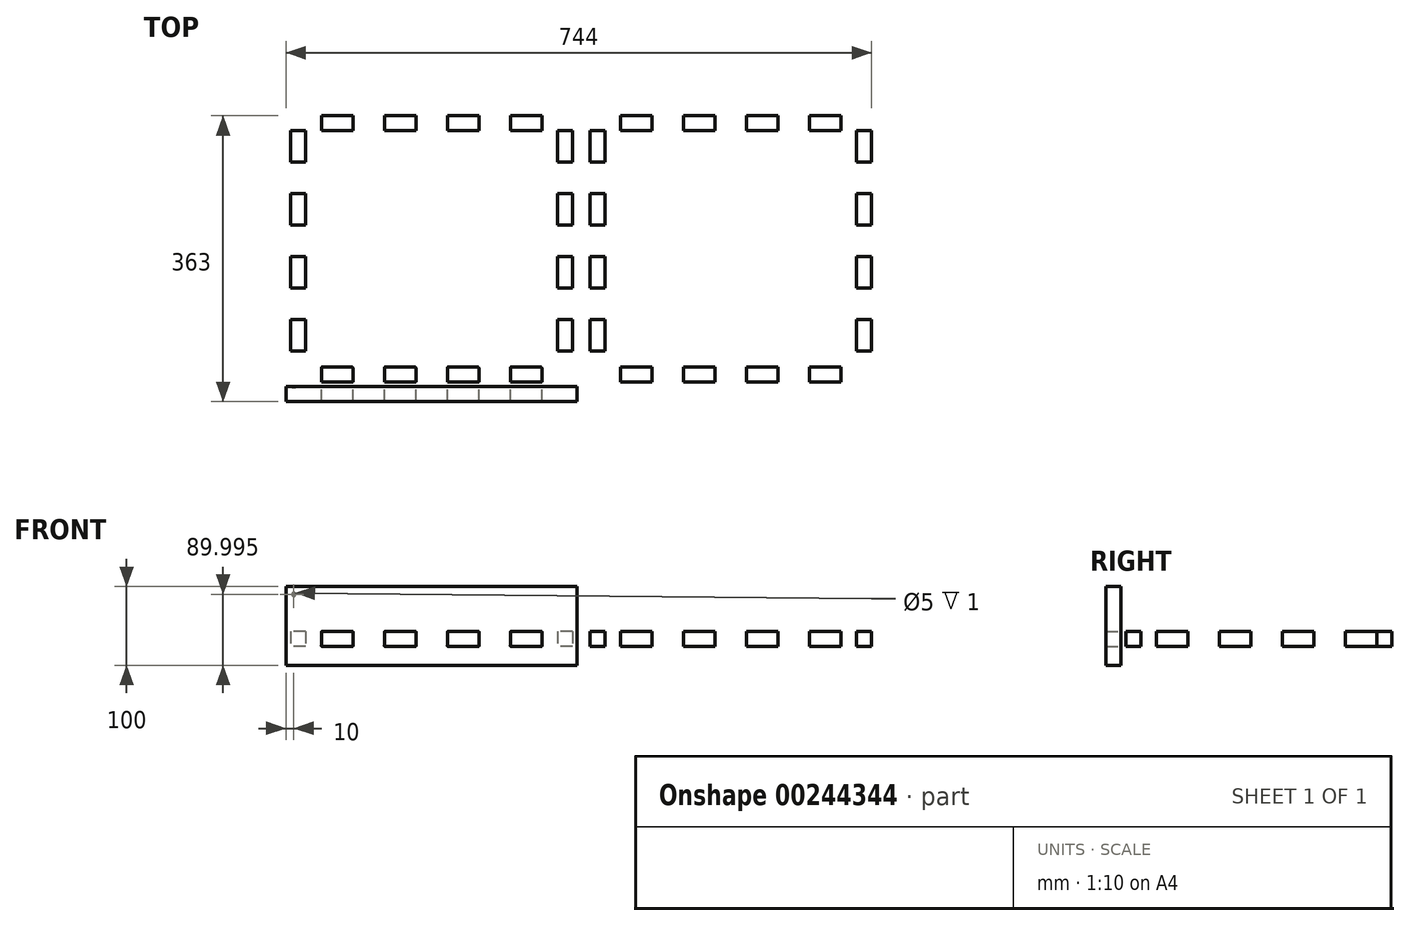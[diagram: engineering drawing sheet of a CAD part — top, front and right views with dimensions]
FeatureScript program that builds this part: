
annotation { "Feature Type Name" : "Feature", "Feature Type Description" : "" }
export const myFeature = defineFeature(function(context is Context, id is Id, definition is map)
    precondition{}
    {
        {
            var Q0;
            Q0=qCreatedBy(makeId("Top.planeOp"),FACE);
            var sketch = newSketch(context, id + "F0", { "sketchPlane" : qUnion([Q0])});
            skLineSegment(sketch, "E0.bottom", {"start": v(25, 25) * mm, "end": v(345, 25) * mm, "construction": true});
            skLineSegment(sketch, "E0.top", {"start": v(25, 325) * mm, "end": v(345, 325) * mm, "construction": true});
            skLineSegment(sketch, "E0.left", {"start": v(25, 25) * mm, "end": v(25, 325) * mm, "construction": true});
            skLineSegment(sketch, "E0.right", {"start": v(345, 25) * mm, "end": v(345, 325) * mm, "construction": true});
            skPoint(sketch, "E1", {"position": v(25, 25) * mm});
            skSolve(sketch);
        }
        {
            var Q0;
            Q0=qCreatedBy(makeId("Top.planeOp"),FACE);
            var sketch = newSketch(context, id + "F1", { "sketchPlane" : qUnion([Q0])});
            skPoint(sketch, "E2", {"position": v(25, 25) * mm});
            skLineSegment(sketch, "E3.bottom", {"start": v(25, 45) * mm, "end": v(6, 45) * mm});
            skLineSegment(sketch, "E3.top", {"start": v(25, 85) * mm, "end": v(6, 85) * mm});
            skLineSegment(sketch, "E3.left", {"start": v(25, 45) * mm, "end": v(25, 85) * mm});
            skLineSegment(sketch, "E3.right", {"start": v(6, 45) * mm, "end": v(6, 85) * mm});
            skLineSegment(sketch, "E4.0.1.0", {"start": v(25, 125) * mm, "end": v(6, 125) * mm});
            skLineSegment(sketch, "E4.0.1.1", {"start": v(6, 125) * mm, "end": v(6, 165) * mm});
            skLineSegment(sketch, "E4.0.1.2", {"start": v(25, 165) * mm, "end": v(6, 165) * mm});
            skLineSegment(sketch, "E4.0.1.3", {"start": v(25, 125) * mm, "end": v(25, 165) * mm});
            skLineSegment(sketch, "E4.0.2.0", {"start": v(25, 205) * mm, "end": v(6, 205) * mm});
            skLineSegment(sketch, "E4.0.2.1", {"start": v(6, 205) * mm, "end": v(6, 245) * mm});
            skLineSegment(sketch, "E4.0.2.2", {"start": v(25, 245) * mm, "end": v(6, 245) * mm});
            skLineSegment(sketch, "E4.0.2.3", {"start": v(25, 205) * mm, "end": v(25, 245) * mm});
            skLineSegment(sketch, "E4.0.3.0", {"start": v(25, 285) * mm, "end": v(6, 285) * mm});
            skLineSegment(sketch, "E4.0.3.1", {"start": v(6, 285) * mm, "end": v(6, 325) * mm});
            skLineSegment(sketch, "E4.0.3.2", {"start": v(25, 325) * mm, "end": v(6, 325) * mm});
            skLineSegment(sketch, "E4.0.3.3", {"start": v(25, 285) * mm, "end": v(25, 325) * mm});
            skLineSegment(sketch, "E4.1.0.0", {"start": v(364, 45) * mm, "end": v(345, 45) * mm});
            skLineSegment(sketch, "E4.1.0.1", {"start": v(345, 45) * mm, "end": v(345, 85) * mm});
            skLineSegment(sketch, "E4.1.0.2", {"start": v(364, 85) * mm, "end": v(345, 85) * mm});
            skLineSegment(sketch, "E4.1.0.3", {"start": v(364, 45) * mm, "end": v(364, 85) * mm});
            skLineSegment(sketch, "E4.1.1.0", {"start": v(364, 125) * mm, "end": v(345, 125) * mm});
            skLineSegment(sketch, "E4.1.1.1", {"start": v(345, 125) * mm, "end": v(345, 165) * mm});
            skLineSegment(sketch, "E4.1.1.2", {"start": v(364, 165) * mm, "end": v(345, 165) * mm});
            skLineSegment(sketch, "E4.1.1.3", {"start": v(364, 125) * mm, "end": v(364, 165) * mm});
            skLineSegment(sketch, "E4.1.2.0", {"start": v(364, 205) * mm, "end": v(345, 205) * mm});
            skLineSegment(sketch, "E4.1.2.1", {"start": v(345, 205) * mm, "end": v(345, 245) * mm});
            skLineSegment(sketch, "E4.1.2.2", {"start": v(364, 245) * mm, "end": v(345, 245) * mm});
            skLineSegment(sketch, "E4.1.2.3", {"start": v(364, 205) * mm, "end": v(364, 245) * mm});
            skLineSegment(sketch, "E4.1.3.0", {"start": v(364, 285) * mm, "end": v(345, 285) * mm});
            skLineSegment(sketch, "E4.1.3.1", {"start": v(345, 285) * mm, "end": v(345, 325) * mm});
            skLineSegment(sketch, "E4.1.3.2", {"start": v(364, 325) * mm, "end": v(345, 325) * mm});
            skLineSegment(sketch, "E4.1.3.3", {"start": v(364, 285) * mm, "end": v(364, 325) * mm});
            skLineSegment(sketch, "E4.direction1", {"start": v(6, 45) * mm, "end": v(345, 45) * mm, "construction": true});
            skLineSegment(sketch, "E4.direction2", {"start": v(6, 45) * mm, "end": v(6, 125) * mm, "construction": true});
            skLineSegment(sketch, "E5.bottom", {"start": v(45, 25) * mm, "end": v(85, 25) * mm});
            skLineSegment(sketch, "E5.top", {"start": v(45, 6) * mm, "end": v(85, 6) * mm});
            skLineSegment(sketch, "E5.left", {"start": v(45, 25) * mm, "end": v(45, 6) * mm});
            skLineSegment(sketch, "E5.right", {"start": v(85, 25) * mm, "end": v(85, 6) * mm});
            skLineSegment(sketch, "E6.0.1.0", {"start": v(45, 344) * mm, "end": v(45, 325) * mm});
            skLineSegment(sketch, "E6.0.1.1", {"start": v(45, 344) * mm, "end": v(85, 344) * mm});
            skLineSegment(sketch, "E6.0.1.2", {"start": v(45, 325) * mm, "end": v(85, 325) * mm});
            skLineSegment(sketch, "E6.0.1.3", {"start": v(85, 344) * mm, "end": v(85, 325) * mm});
            skLineSegment(sketch, "E6.1.0.0", {"start": v(125, 25) * mm, "end": v(125, 6) * mm});
            skLineSegment(sketch, "E6.1.0.1", {"start": v(125, 25) * mm, "end": v(165, 25) * mm});
            skLineSegment(sketch, "E6.1.0.2", {"start": v(125, 6) * mm, "end": v(165, 6) * mm});
            skLineSegment(sketch, "E6.1.0.3", {"start": v(165, 25) * mm, "end": v(165, 6) * mm});
            skLineSegment(sketch, "E6.1.1.0", {"start": v(125, 344) * mm, "end": v(125, 325) * mm});
            skLineSegment(sketch, "E6.1.1.1", {"start": v(125, 344) * mm, "end": v(165, 344) * mm});
            skLineSegment(sketch, "E6.1.1.2", {"start": v(125, 325) * mm, "end": v(165, 325) * mm});
            skLineSegment(sketch, "E6.1.1.3", {"start": v(165, 344) * mm, "end": v(165, 325) * mm});
            skLineSegment(sketch, "E6.2.0.0", {"start": v(205, 25) * mm, "end": v(205, 6) * mm});
            skLineSegment(sketch, "E6.2.0.1", {"start": v(205, 25) * mm, "end": v(245, 25) * mm});
            skLineSegment(sketch, "E6.2.0.2", {"start": v(205, 6) * mm, "end": v(245, 6) * mm});
            skLineSegment(sketch, "E6.2.0.3", {"start": v(245, 25) * mm, "end": v(245, 6) * mm});
            skLineSegment(sketch, "E6.2.1.0", {"start": v(205, 344) * mm, "end": v(205, 325) * mm});
            skLineSegment(sketch, "E6.2.1.1", {"start": v(205, 344) * mm, "end": v(245, 344) * mm});
            skLineSegment(sketch, "E6.2.1.2", {"start": v(205, 325) * mm, "end": v(245, 325) * mm});
            skLineSegment(sketch, "E6.2.1.3", {"start": v(245, 344) * mm, "end": v(245, 325) * mm});
            skLineSegment(sketch, "E6.3.0.0", {"start": v(285, 25) * mm, "end": v(285, 6) * mm});
            skLineSegment(sketch, "E6.3.0.1", {"start": v(285, 25) * mm, "end": v(325, 25) * mm});
            skLineSegment(sketch, "E6.3.0.2", {"start": v(285, 6) * mm, "end": v(325, 6) * mm});
            skLineSegment(sketch, "E6.3.0.3", {"start": v(325, 25) * mm, "end": v(325, 6) * mm});
            skLineSegment(sketch, "E6.3.1.0", {"start": v(285, 344) * mm, "end": v(285, 325) * mm});
            skLineSegment(sketch, "E6.3.1.1", {"start": v(285, 344) * mm, "end": v(325, 344) * mm});
            skLineSegment(sketch, "E6.3.1.2", {"start": v(285, 325) * mm, "end": v(325, 325) * mm});
            skLineSegment(sketch, "E6.3.1.3", {"start": v(325, 344) * mm, "end": v(325, 325) * mm});
            skLineSegment(sketch, "E6.direction1", {"start": v(45, 6) * mm, "end": v(125, 6) * mm, "construction": true});
            skLineSegment(sketch, "E6.direction2", {"start": v(45, 6) * mm, "end": v(45, 325) * mm, "construction": true});
            skLineSegment(sketch, "E7.bottom", {"start": v(25, 325) * mm, "end": v(345, 325) * mm});
            skLineSegment(sketch, "E7.top", {"start": v(25, 25) * mm, "end": v(345, 25) * mm});
            skLineSegment(sketch, "E7.left", {"start": v(25, 325) * mm, "end": v(25, 25) * mm});
            skLineSegment(sketch, "E7.right", {"start": v(345, 325) * mm, "end": v(345, 25) * mm});
            skLineSegment(sketch, "E8", {"start": v(540.47, -44.7) * mm, "end": v(540.47, -111.64) * mm, "construction": true});
            skSolve(sketch);
        }
        {
            var Q0;
            {var subQ0=sQuery(id+"F1.wireOp",EDGE,"E3.bottom");Q0=makeQuery(id+"F1.imprint","IMPRINT",FACE,{"disambiguationData":[TD([[makeQuery(id+"F1.imprint","IMPRINT",EDGE,{"derivedFrom":subQ0}),-1.0]])]});}
            var Q1;
            {var subQ0=sQuery(id+"F1.wireOp",EDGE,"E4.0.1.0");Q1=makeQuery(id+"F1.imprint","IMPRINT",FACE,{"disambiguationData":[TD([[makeQuery(id+"F1.imprint","IMPRINT",EDGE,{"derivedFrom":subQ0}),-1.0]])]});}
            var Q2;
            {var subQ15=sQuery(id+"F1.wireOp",EDGE,"E7.bottom");var subQ31=makeQuery(id+"F1.imprint","INTERSECT",VERTEX,{"derivedFrom":[sQuery(id+"F1.wireOp",EDGE,"E6.0.1.0"),subQ15]});Q2=makeQuery(id+"F1.imprint","IMPRINT",FACE,{"disambiguationData":[TD([[makeQuery(id+"F1.imprint","IMPRINT",EDGE,{"disambiguationData":[TD([[subQ31,-1.0]])],"derivedFrom":subQ15}),-1.0]])]});}
            var Q3;
            {var subQ0=sQuery(id+"F1.wireOp",EDGE,"E4.1.0.0");Q3=makeQuery(id+"F1.imprint","IMPRINT",FACE,{"disambiguationData":[TD([[makeQuery(id+"F1.imprint","IMPRINT",EDGE,{"derivedFrom":subQ0}),-1.0]])]});}
            var Q4;
            {var subQ0=sQuery(id+"F1.wireOp",EDGE,"E6.3.1.0");Q4=makeQuery(id+"F1.imprint","IMPRINT",FACE,{"disambiguationData":[TD([[makeQuery(id+"F1.imprint","IMPRINT",EDGE,{"derivedFrom":subQ0}),1.0]])]});}
            var Q5;
            {var subQ0=sQuery(id+"F1.wireOp",EDGE,"E4.0.2.0");Q5=makeQuery(id+"F1.imprint","IMPRINT",FACE,{"disambiguationData":[TD([[makeQuery(id+"F1.imprint","IMPRINT",EDGE,{"derivedFrom":subQ0}),-1.0]])]});}
            var Q6;
            {var subQ0=sQuery(id+"F1.wireOp",EDGE,"E4.0.3.0");Q6=makeQuery(id+"F1.imprint","IMPRINT",FACE,{"disambiguationData":[TD([[makeQuery(id+"F1.imprint","IMPRINT",EDGE,{"derivedFrom":subQ0}),-1.0]])]});}
            var Q7;
            {var subQ0=sQuery(id+"F1.wireOp",EDGE,"E4.1.2.0");Q7=makeQuery(id+"F1.imprint","IMPRINT",FACE,{"disambiguationData":[TD([[makeQuery(id+"F1.imprint","IMPRINT",EDGE,{"derivedFrom":subQ0}),-1.0]])]});}
            var Q8;
            {var subQ0=sQuery(id+"F1.wireOp",EDGE,"E4.1.1.0");Q8=makeQuery(id+"F1.imprint","IMPRINT",FACE,{"disambiguationData":[TD([[makeQuery(id+"F1.imprint","IMPRINT",EDGE,{"derivedFrom":subQ0}),-1.0]])]});}
            var Q9;
            {var subQ0=sQuery(id+"F1.wireOp",EDGE,"E6.3.0.0");Q9=makeQuery(id+"F1.imprint","IMPRINT",FACE,{"disambiguationData":[TD([[makeQuery(id+"F1.imprint","IMPRINT",EDGE,{"derivedFrom":subQ0}),1.0]])]});}
            var Q10;
            {var subQ0=sQuery(id+"F1.wireOp",EDGE,"E6.2.0.0");Q10=makeQuery(id+"F1.imprint","IMPRINT",FACE,{"disambiguationData":[TD([[makeQuery(id+"F1.imprint","IMPRINT",EDGE,{"derivedFrom":subQ0}),1.0]])]});}
            var Q11;
            {var subQ0=sQuery(id+"F1.wireOp",EDGE,"E6.1.1.0");Q11=makeQuery(id+"F1.imprint","IMPRINT",FACE,{"disambiguationData":[TD([[makeQuery(id+"F1.imprint","IMPRINT",EDGE,{"derivedFrom":subQ0}),1.0]])]});}
            var Q12;
            {var subQ0=sQuery(id+"F1.wireOp",EDGE,"E6.2.1.0");Q12=makeQuery(id+"F1.imprint","IMPRINT",FACE,{"disambiguationData":[TD([[makeQuery(id+"F1.imprint","IMPRINT",EDGE,{"derivedFrom":subQ0}),1.0]])]});}
            var Q13;
            {var subQ0=sQuery(id+"F1.wireOp",EDGE,"E6.1.0.0");Q13=makeQuery(id+"F1.imprint","IMPRINT",FACE,{"disambiguationData":[TD([[makeQuery(id+"F1.imprint","IMPRINT",EDGE,{"derivedFrom":subQ0}),1.0]])]});}
            var Q14;
            Q14=makeQuery(id+"F1.imprint","IMPRINT",FACE,{"disambiguationData":[TD([[makeQuery(id+"F1.imprint","IMPRINT",EDGE,{"derivedFrom":sQuery(id+"F1.wireOp",EDGE,"E5.top")}),1.0]])]});
            var Q15;
            {var subQ0=sQuery(id+"F1.wireOp",EDGE,"E6.0.1.0");Q15=makeQuery(id+"F1.imprint","IMPRINT",FACE,{"disambiguationData":[TD([[makeQuery(id+"F1.imprint","IMPRINT",EDGE,{"derivedFrom":subQ0}),1.0]])]});}
            var Q16;
            {var subQ0=sQuery(id+"F1.wireOp",EDGE,"E4.1.3.0");Q16=makeQuery(id+"F1.imprint","IMPRINT",FACE,{"disambiguationData":[TD([[makeQuery(id+"F1.imprint","IMPRINT",EDGE,{"derivedFrom":subQ0}),-1.0]])]});}
            extrude(context, id + "F2", {"entities" : qUnion([Q0, Q1, Q2, Q3, Q4, Q5, Q6, Q7, Q8, Q9, Q10, Q11, Q12, Q13, Q14, Q15, Q16]), "depth" : 19 * mm});
        }
        {
            var Q0;
            Q0=makeQuery(id+"F2.opExtrude","SWEPT_BODY",BODY,{"disambiguationData":[OSD([sQuery(id+"F1.wireOp",EDGE,"E3.bottom"),sQuery(id+"F1.wireOp",EDGE,"E3.top"),sQuery(id+"F1.wireOp",EDGE,"E3.right"),sQuery(id+"F1.wireOp",EDGE,"E4.0.1.0"),sQuery(id+"F1.wireOp",EDGE,"E4.0.1.1"),sQuery(id+"F1.wireOp",EDGE,"E4.0.1.2"),sQuery(id+"F1.wireOp",EDGE,"E4.0.2.0"),sQuery(id+"F1.wireOp",EDGE,"E4.0.2.1"),sQuery(id+"F1.wireOp",EDGE,"E4.0.2.2"),sQuery(id+"F1.wireOp",EDGE,"E4.0.3.0"),sQuery(id+"F1.wireOp",EDGE,"E4.0.3.1"),sQuery(id+"F1.wireOp",EDGE,"E4.0.3.2"),sQuery(id+"F1.wireOp",EDGE,"E4.1.0.0"),sQuery(id+"F1.wireOp",EDGE,"E4.1.0.2"),sQuery(id+"F1.wireOp",EDGE,"E4.1.0.3"),sQuery(id+"F1.wireOp",EDGE,"E4.1.1.0"),sQuery(id+"F1.wireOp",EDGE,"E4.1.1.2"),sQuery(id+"F1.wireOp",EDGE,"E4.1.1.3"),sQuery(id+"F1.wireOp",EDGE,"E4.1.2.0"),sQuery(id+"F1.wireOp",EDGE,"E4.1.2.2"),sQuery(id+"F1.wireOp",EDGE,"E4.1.2.3"),sQuery(id+"F1.wireOp",EDGE,"E4.1.3.0"),sQuery(id+"F1.wireOp",EDGE,"E4.1.3.2"),sQuery(id+"F1.wireOp",EDGE,"E4.1.3.3"),sQuery(id+"F1.wireOp",EDGE,"E5.top"),sQuery(id+"F1.wireOp",EDGE,"E5.left"),sQuery(id+"F1.wireOp",EDGE,"E5.right"),sQuery(id+"F1.wireOp",EDGE,"E6.0.1.0"),sQuery(id+"F1.wireOp",EDGE,"E6.0.1.1"),sQuery(id+"F1.wireOp",EDGE,"E6.0.1.3"),sQuery(id+"F1.wireOp",EDGE,"E6.1.0.0"),sQuery(id+"F1.wireOp",EDGE,"E6.1.0.2"),sQuery(id+"F1.wireOp",EDGE,"E6.1.0.3"),sQuery(id+"F1.wireOp",EDGE,"E6.1.1.0"),sQuery(id+"F1.wireOp",EDGE,"E6.1.1.1"),sQuery(id+"F1.wireOp",EDGE,"E6.1.1.3"),sQuery(id+"F1.wireOp",EDGE,"E6.2.0.0"),sQuery(id+"F1.wireOp",EDGE,"E6.2.0.2"),sQuery(id+"F1.wireOp",EDGE,"E6.2.0.3"),sQuery(id+"F1.wireOp",EDGE,"E6.2.1.0"),sQuery(id+"F1.wireOp",EDGE,"E6.2.1.1"),sQuery(id+"F1.wireOp",EDGE,"E6.2.1.3"),sQuery(id+"F1.wireOp",EDGE,"E6.3.0.0"),sQuery(id+"F1.wireOp",EDGE,"E6.3.0.2"),sQuery(id+"F1.wireOp",EDGE,"E6.3.0.3"),sQuery(id+"F1.wireOp",EDGE,"E6.3.1.0"),sQuery(id+"F1.wireOp",EDGE,"E6.3.1.1"),sQuery(id+"F1.wireOp",EDGE,"E6.3.1.3"),sQuery(id+"F1.wireOp",EDGE,"E7.bottom"),sQuery(id+"F1.wireOp",EDGE,"E7.top"),sQuery(id+"F1.wireOp",EDGE,"E7.left"),sQuery(id+"F1.wireOp",EDGE,"E7.right")])]});
            transform(context, id + "F3", {"entities" : qUnion([Q0]), "transformType" : TransformType.TRANSLATION_3D, "dx" : 380 * mm, "dy" : 0 * mm, "dz" : 0 * mm, "makeCopy" : true});
        }
        {
            var Q0;
            Q0=qCreatedBy(makeId("Front.planeOp"),FACE);
            var sketch = newSketch(context, id + "F4", { "sketchPlane" : qUnion([Q0])});
            skLineSegment(sketch, "E9.bottom", {"start": v(0, -23.82) * mm, "end": v(370, -23.82) * mm});
            skLineSegment(sketch, "E9.top", {"start": v(0, 76.18) * mm, "end": v(370, 76.18) * mm});
            skLineSegment(sketch, "E9.left", {"start": v(0, -23.82) * mm, "end": v(0, 76.18) * mm});
            skLineSegment(sketch, "E9.right", {"start": v(370, -23.82) * mm, "end": v(370, 76.18) * mm});
            skSolve(sketch);
        }
        {
            var Q0;
            Q0=makeQuery(id+"F4.imprint","IMPRINT",FACE,{"disambiguationData":[TD([[makeQuery(id+"F4.imprint","IMPRINT",EDGE,{"derivedFrom":sQuery(id+"F4.wireOp",EDGE,"E9.bottom")}),1.0]])]});
            extrude(context, id + "F5", {"entities" : qUnion([Q0]), "depth" : 19 * mm});
        }
        {
            var Q0;
            Q0=makeQuery(id+"F2.opExtrude","SWEPT_FACE",FACE,{"disambiguationData":[OSD([sQuery(id+"F1.wireOp",EDGE,"E5.top")])]});
            var Q1;
            Q1=makeQuery(id+"F2.opExtrude","SWEPT_FACE",FACE,{"disambiguationData":[OSD([sQuery(id+"F1.wireOp",EDGE,"E6.1.0.2")])]});
            var Q2;
            Q2=makeQuery(id+"F2.opExtrude","SWEPT_FACE",FACE,{"disambiguationData":[OSD([sQuery(id+"F1.wireOp",EDGE,"E6.2.0.2")])]});
            var Q3;
            Q3=makeQuery(id+"F2.opExtrude","SWEPT_FACE",FACE,{"disambiguationData":[OSD([sQuery(id+"F1.wireOp",EDGE,"E6.3.0.2")])]});
            extrude(context, id + "F6", {"entities" : qUnion([Q0, Q1, Q2, Q3]), "operationType" : NewBodyOperationType.REMOVE, "depth" : 188 * mm});
        }
        {
            var Q0;
            Q0=makeQuery(id+"F6.boolean.opBoolean","INTERSECT",EDGE,{"derivedFrom":[makeQuery(id+"F5.opExtrude","CAP_FACE",FACE,{"disambiguationData":[OSD([sQuery(id+"F4.wireOp",EDGE,"E9.bottom"),sQuery(id+"F4.wireOp",EDGE,"E9.top"),sQuery(id+"F4.wireOp",EDGE,"E9.left"),sQuery(id+"F4.wireOp",EDGE,"E9.right")])],"isStart":true}),makeQuery(id+"F6.opExtrude","SWEPT_FACE",FACE,{"disambiguationData":[OSD([sQuery(id+"F1.wireOp",EDGE,"E6.3.0.2"),sQuery(id+"F1.wireOp",EDGE,"E6.3.0.3")])]})]});
            var Q1;
            Q1=makeQuery(id+"F6.boolean.opBoolean","INTERSECT",EDGE,{"derivedFrom":[makeQuery(id+"F5.opExtrude","CAP_FACE",FACE,{"disambiguationData":[OSD([sQuery(id+"F4.wireOp",EDGE,"E9.bottom"),sQuery(id+"F4.wireOp",EDGE,"E9.top"),sQuery(id+"F4.wireOp",EDGE,"E9.left"),sQuery(id+"F4.wireOp",EDGE,"E9.right")])],"isStart":true}),makeQuery(id+"F6.opExtrude","SWEPT_FACE",FACE,{"disambiguationData":[OSD([sQuery(id+"F1.wireOp",EDGE,"E6.3.0.0"),sQuery(id+"F1.wireOp",EDGE,"E6.3.0.2")])]})]});
            var Q2;
            Q2=makeQuery(id+"F6.boolean.opBoolean","INTERSECT",EDGE,{"derivedFrom":[makeQuery(id+"F5.opExtrude","CAP_FACE",FACE,{"disambiguationData":[OSD([sQuery(id+"F4.wireOp",EDGE,"E9.bottom"),sQuery(id+"F4.wireOp",EDGE,"E9.top"),sQuery(id+"F4.wireOp",EDGE,"E9.left"),sQuery(id+"F4.wireOp",EDGE,"E9.right")])],"isStart":true}),makeQuery(id+"F6.opExtrude","SWEPT_FACE",FACE,{"disambiguationData":[OSD([sQuery(id+"F1.wireOp",EDGE,"E6.2.0.2"),sQuery(id+"F1.wireOp",EDGE,"E6.2.0.3")])]})]});
            var Q3;
            Q3=makeQuery(id+"F6.boolean.opBoolean","INTERSECT",EDGE,{"derivedFrom":[makeQuery(id+"F5.opExtrude","CAP_FACE",FACE,{"disambiguationData":[OSD([sQuery(id+"F4.wireOp",EDGE,"E9.bottom"),sQuery(id+"F4.wireOp",EDGE,"E9.top"),sQuery(id+"F4.wireOp",EDGE,"E9.left"),sQuery(id+"F4.wireOp",EDGE,"E9.right")])],"isStart":true}),makeQuery(id+"F6.opExtrude","SWEPT_FACE",FACE,{"disambiguationData":[OSD([sQuery(id+"F1.wireOp",EDGE,"E6.2.0.0"),sQuery(id+"F1.wireOp",EDGE,"E6.2.0.2")])]})]});
            var Q4;
            Q4=makeQuery(id+"F6.boolean.opBoolean","INTERSECT",EDGE,{"derivedFrom":[makeQuery(id+"F5.opExtrude","CAP_FACE",FACE,{"disambiguationData":[OSD([sQuery(id+"F4.wireOp",EDGE,"E9.bottom"),sQuery(id+"F4.wireOp",EDGE,"E9.top"),sQuery(id+"F4.wireOp",EDGE,"E9.left"),sQuery(id+"F4.wireOp",EDGE,"E9.right")])],"isStart":true}),makeQuery(id+"F6.opExtrude","SWEPT_FACE",FACE,{"disambiguationData":[OSD([sQuery(id+"F1.wireOp",EDGE,"E6.1.0.2"),sQuery(id+"F1.wireOp",EDGE,"E6.1.0.3")])]})]});
            var Q5;
            Q5=makeQuery(id+"F6.boolean.opBoolean","INTERSECT",EDGE,{"derivedFrom":[makeQuery(id+"F5.opExtrude","CAP_FACE",FACE,{"disambiguationData":[OSD([sQuery(id+"F4.wireOp",EDGE,"E9.bottom"),sQuery(id+"F4.wireOp",EDGE,"E9.top"),sQuery(id+"F4.wireOp",EDGE,"E9.left"),sQuery(id+"F4.wireOp",EDGE,"E9.right")])],"isStart":true}),makeQuery(id+"F6.opExtrude","SWEPT_FACE",FACE,{"disambiguationData":[OSD([sQuery(id+"F1.wireOp",EDGE,"E6.1.0.0"),sQuery(id+"F1.wireOp",EDGE,"E6.1.0.2")])]})]});
            var Q6;
            Q6=makeQuery(id+"F6.boolean.opBoolean","INTERSECT",EDGE,{"derivedFrom":[makeQuery(id+"F5.opExtrude","CAP_FACE",FACE,{"disambiguationData":[OSD([sQuery(id+"F4.wireOp",EDGE,"E9.bottom"),sQuery(id+"F4.wireOp",EDGE,"E9.top"),sQuery(id+"F4.wireOp",EDGE,"E9.left"),sQuery(id+"F4.wireOp",EDGE,"E9.right")])],"isStart":true}),makeQuery(id+"F6.opExtrude","SWEPT_FACE",FACE,{"disambiguationData":[OSD([sQuery(id+"F1.wireOp",EDGE,"E5.top"),sQuery(id+"F1.wireOp",EDGE,"E5.right")])]})]});
            var Q7;
            Q7=makeQuery(id+"F6.boolean.opBoolean","INTERSECT",EDGE,{"derivedFrom":[makeQuery(id+"F5.opExtrude","CAP_FACE",FACE,{"disambiguationData":[OSD([sQuery(id+"F4.wireOp",EDGE,"E9.bottom"),sQuery(id+"F4.wireOp",EDGE,"E9.top"),sQuery(id+"F4.wireOp",EDGE,"E9.left"),sQuery(id+"F4.wireOp",EDGE,"E9.right")])],"isStart":true}),makeQuery(id+"F6.opExtrude","SWEPT_FACE",FACE,{"disambiguationData":[OSD([sQuery(id+"F1.wireOp",EDGE,"E5.top"),sQuery(id+"F1.wireOp",EDGE,"E5.left")])]})]});
            fillet(context, id + "F7", {"entities" : qUnion([Q0, Q1, Q2, Q3, Q4, Q5, Q6, Q7]), "radius" : 1.5 * mm, "tangentPropagation" : true, "allowEdgeOverflow" : false});
        }
        {
            var Q0;
            {var subQ0=sQuery(id+"F1.wireOp",EDGE,"E5.left");var subQ1=sQuery(id+"F1.wireOp",EDGE,"E5.top");Q0=makeQuery(id+"F6.boolean.opBoolean","COPY",EDGE,{"derivedFrom":makeQuery(id+"F6.opExtrude","SWEPT_EDGE",EDGE,{"disambiguationData":[OSD([subQ1,subQ0]),TDD([makeQuery(id+"F2.opExtrude","CAP_VERTEX",VERTEX,{"disambiguationData":[OSD([subQ1,subQ0])],"isStart":false})])]})});}
            var Q1;
            {var subQ0=sQuery(id+"F1.wireOp",EDGE,"E5.left");var subQ1=sQuery(id+"F1.wireOp",EDGE,"E5.top");Q1=makeQuery(id+"F6.boolean.opBoolean","COPY",EDGE,{"derivedFrom":makeQuery(id+"F6.opExtrude","SWEPT_EDGE",EDGE,{"disambiguationData":[OSD([subQ1,subQ0]),TDD([makeQuery(id+"F2.opExtrude","CAP_VERTEX",VERTEX,{"disambiguationData":[OSD([subQ1,subQ0])],"isStart":true})])]})});}
            var Q2;
            {var subQ0=sQuery(id+"F1.wireOp",EDGE,"E5.right");var subQ1=sQuery(id+"F1.wireOp",EDGE,"E5.top");Q2=makeQuery(id+"F6.boolean.opBoolean","COPY",EDGE,{"derivedFrom":makeQuery(id+"F6.opExtrude","SWEPT_EDGE",EDGE,{"disambiguationData":[OSD([subQ1,subQ0]),TDD([makeQuery(id+"F2.opExtrude","CAP_VERTEX",VERTEX,{"disambiguationData":[OSD([subQ1,subQ0])],"isStart":false})])]})});}
            var Q3;
            {var subQ0=sQuery(id+"F1.wireOp",EDGE,"E5.right");var subQ1=sQuery(id+"F1.wireOp",EDGE,"E5.top");Q3=makeQuery(id+"F6.boolean.opBoolean","COPY",EDGE,{"derivedFrom":makeQuery(id+"F6.opExtrude","SWEPT_EDGE",EDGE,{"disambiguationData":[OSD([subQ1,subQ0]),TDD([makeQuery(id+"F2.opExtrude","CAP_VERTEX",VERTEX,{"disambiguationData":[OSD([subQ1,subQ0])],"isStart":true})])]})});}
            var Q4;
            {var subQ0=sQuery(id+"F1.wireOp",EDGE,"E6.1.0.2");var subQ1=sQuery(id+"F1.wireOp",EDGE,"E6.1.0.0");Q4=makeQuery(id+"F6.boolean.opBoolean","COPY",EDGE,{"derivedFrom":makeQuery(id+"F6.opExtrude","SWEPT_EDGE",EDGE,{"disambiguationData":[OSD([subQ1,subQ0]),TDD([makeQuery(id+"F2.opExtrude","CAP_VERTEX",VERTEX,{"disambiguationData":[OSD([subQ1,subQ0])],"isStart":false})])]})});}
            var Q5;
            {var subQ0=sQuery(id+"F1.wireOp",EDGE,"E6.1.0.2");var subQ1=sQuery(id+"F1.wireOp",EDGE,"E6.1.0.0");Q5=makeQuery(id+"F6.boolean.opBoolean","COPY",EDGE,{"derivedFrom":makeQuery(id+"F6.opExtrude","SWEPT_EDGE",EDGE,{"disambiguationData":[OSD([subQ1,subQ0]),TDD([makeQuery(id+"F2.opExtrude","CAP_VERTEX",VERTEX,{"disambiguationData":[OSD([subQ1,subQ0])],"isStart":true})])]})});}
            var Q6;
            {var subQ0=sQuery(id+"F1.wireOp",EDGE,"E6.1.0.3");var subQ1=sQuery(id+"F1.wireOp",EDGE,"E6.1.0.2");Q6=makeQuery(id+"F6.boolean.opBoolean","COPY",EDGE,{"derivedFrom":makeQuery(id+"F6.opExtrude","SWEPT_EDGE",EDGE,{"disambiguationData":[OSD([subQ1,subQ0]),TDD([makeQuery(id+"F2.opExtrude","CAP_VERTEX",VERTEX,{"disambiguationData":[OSD([subQ1,subQ0])],"isStart":true})])]})});}
            var Q7;
            {var subQ0=sQuery(id+"F1.wireOp",EDGE,"E6.2.0.2");var subQ1=sQuery(id+"F1.wireOp",EDGE,"E6.2.0.0");Q7=makeQuery(id+"F6.boolean.opBoolean","COPY",EDGE,{"derivedFrom":makeQuery(id+"F6.opExtrude","SWEPT_EDGE",EDGE,{"disambiguationData":[OSD([subQ1,subQ0]),TDD([makeQuery(id+"F2.opExtrude","CAP_VERTEX",VERTEX,{"disambiguationData":[OSD([subQ1,subQ0])],"isStart":true})])]})});}
            var Q8;
            {var subQ0=sQuery(id+"F1.wireOp",EDGE,"E6.2.0.2");var subQ1=sQuery(id+"F1.wireOp",EDGE,"E6.2.0.0");Q8=makeQuery(id+"F6.boolean.opBoolean","COPY",EDGE,{"derivedFrom":makeQuery(id+"F6.opExtrude","SWEPT_EDGE",EDGE,{"disambiguationData":[OSD([subQ1,subQ0]),TDD([makeQuery(id+"F2.opExtrude","CAP_VERTEX",VERTEX,{"disambiguationData":[OSD([subQ1,subQ0])],"isStart":false})])]})});}
            var Q9;
            {var subQ0=sQuery(id+"F1.wireOp",EDGE,"E6.2.0.3");var subQ1=sQuery(id+"F1.wireOp",EDGE,"E6.2.0.2");Q9=makeQuery(id+"F6.boolean.opBoolean","COPY",EDGE,{"derivedFrom":makeQuery(id+"F6.opExtrude","SWEPT_EDGE",EDGE,{"disambiguationData":[OSD([subQ1,subQ0]),TDD([makeQuery(id+"F2.opExtrude","CAP_VERTEX",VERTEX,{"disambiguationData":[OSD([subQ1,subQ0])],"isStart":true})])]})});}
            var Q10;
            {var subQ0=sQuery(id+"F1.wireOp",EDGE,"E6.2.0.3");var subQ1=sQuery(id+"F1.wireOp",EDGE,"E6.2.0.2");Q10=makeQuery(id+"F6.boolean.opBoolean","COPY",EDGE,{"derivedFrom":makeQuery(id+"F6.opExtrude","SWEPT_EDGE",EDGE,{"disambiguationData":[OSD([subQ1,subQ0]),TDD([makeQuery(id+"F2.opExtrude","CAP_VERTEX",VERTEX,{"disambiguationData":[OSD([subQ1,subQ0])],"isStart":false})])]})});}
            var Q11;
            {var subQ0=sQuery(id+"F1.wireOp",EDGE,"E6.3.0.3");var subQ1=sQuery(id+"F1.wireOp",EDGE,"E6.3.0.2");Q11=makeQuery(id+"F6.boolean.opBoolean","COPY",EDGE,{"derivedFrom":makeQuery(id+"F6.opExtrude","SWEPT_EDGE",EDGE,{"disambiguationData":[OSD([subQ1,subQ0]),TDD([makeQuery(id+"F2.opExtrude","CAP_VERTEX",VERTEX,{"disambiguationData":[OSD([subQ1,subQ0])],"isStart":false})])]})});}
            var Q12;
            {var subQ0=sQuery(id+"F1.wireOp",EDGE,"E6.3.0.2");var subQ1=sQuery(id+"F1.wireOp",EDGE,"E6.3.0.0");Q12=makeQuery(id+"F6.boolean.opBoolean","COPY",EDGE,{"derivedFrom":makeQuery(id+"F6.opExtrude","SWEPT_EDGE",EDGE,{"disambiguationData":[OSD([subQ1,subQ0]),TDD([makeQuery(id+"F2.opExtrude","CAP_VERTEX",VERTEX,{"disambiguationData":[OSD([subQ1,subQ0])],"isStart":false})])]})});}
            var Q13;
            {var subQ0=sQuery(id+"F1.wireOp",EDGE,"E6.1.0.3");var subQ1=sQuery(id+"F1.wireOp",EDGE,"E6.1.0.2");Q13=makeQuery(id+"F6.boolean.opBoolean","COPY",EDGE,{"derivedFrom":makeQuery(id+"F6.opExtrude","SWEPT_EDGE",EDGE,{"disambiguationData":[OSD([subQ1,subQ0]),TDD([makeQuery(id+"F2.opExtrude","CAP_VERTEX",VERTEX,{"disambiguationData":[OSD([subQ1,subQ0])],"isStart":false})])]})});}
            var Q14;
            {var subQ0=sQuery(id+"F1.wireOp",EDGE,"E6.3.0.2");var subQ1=sQuery(id+"F1.wireOp",EDGE,"E6.3.0.0");Q14=makeQuery(id+"F6.boolean.opBoolean","COPY",EDGE,{"derivedFrom":makeQuery(id+"F6.opExtrude","SWEPT_EDGE",EDGE,{"disambiguationData":[OSD([subQ1,subQ0]),TDD([makeQuery(id+"F2.opExtrude","CAP_VERTEX",VERTEX,{"disambiguationData":[OSD([subQ1,subQ0])],"isStart":true})])]})});}
            var Q15;
            {var subQ0=sQuery(id+"F1.wireOp",EDGE,"E6.3.0.3");var subQ1=sQuery(id+"F1.wireOp",EDGE,"E6.3.0.2");Q15=makeQuery(id+"F6.boolean.opBoolean","COPY",EDGE,{"derivedFrom":makeQuery(id+"F6.opExtrude","SWEPT_EDGE",EDGE,{"disambiguationData":[OSD([subQ1,subQ0]),TDD([makeQuery(id+"F2.opExtrude","CAP_VERTEX",VERTEX,{"disambiguationData":[OSD([subQ1,subQ0])],"isStart":true})])]})});}
            fillet(context, id + "F8", {"entities" : qUnion([Q0, Q1, Q2, Q3, Q4, Q5, Q6, Q7, Q8, Q9, Q10, Q11, Q12, Q13, Q14, Q15]), "radius" : 1.5 * mm, "tangentPropagation" : true, "allowEdgeOverflow" : false});
        }
        {
            var Q0;
            Q0=makeQuery(id+"F2.opExtrude","CAP_EDGE",EDGE,{"disambiguationData":[OSD([sQuery(id+"F1.wireOp",EDGE,"E5.left")])],"isStart":false});
            var Q1;
            Q1=makeQuery(id+"F2.opExtrude","CAP_EDGE",EDGE,{"disambiguationData":[OSD([sQuery(id+"F1.wireOp",EDGE,"E5.right")])],"isStart":false});
            var Q2;
            Q2=makeQuery(id+"F2.opExtrude","CAP_EDGE",EDGE,{"disambiguationData":[OSD([sQuery(id+"F1.wireOp",EDGE,"E6.1.0.0")])],"isStart":false});
            var Q3;
            Q3=makeQuery(id+"F2.opExtrude","CAP_EDGE",EDGE,{"disambiguationData":[OSD([sQuery(id+"F1.wireOp",EDGE,"E6.1.0.3")])],"isStart":false});
            var Q4;
            Q4=makeQuery(id+"F2.opExtrude","CAP_EDGE",EDGE,{"disambiguationData":[OSD([sQuery(id+"F1.wireOp",EDGE,"E6.2.0.0")])],"isStart":false});
            var Q5;
            Q5=makeQuery(id+"F2.opExtrude","CAP_EDGE",EDGE,{"disambiguationData":[OSD([sQuery(id+"F1.wireOp",EDGE,"E6.2.0.3")])],"isStart":false});
            var Q6;
            Q6=makeQuery(id+"F2.opExtrude","CAP_EDGE",EDGE,{"disambiguationData":[OSD([sQuery(id+"F1.wireOp",EDGE,"E6.3.0.0")])],"isStart":false});
            var Q7;
            Q7=makeQuery(id+"F2.opExtrude","CAP_EDGE",EDGE,{"disambiguationData":[OSD([sQuery(id+"F1.wireOp",EDGE,"E6.3.0.3")])],"isStart":false});
            var Q8;
            Q8=makeQuery(id+"F2.opExtrude","CAP_EDGE",EDGE,{"disambiguationData":[OSD([sQuery(id+"F1.wireOp",EDGE,"E5.left")])],"isStart":true});
            var Q9;
            Q9=makeQuery(id+"F2.opExtrude","CAP_EDGE",EDGE,{"disambiguationData":[OSD([sQuery(id+"F1.wireOp",EDGE,"E5.right")])],"isStart":true});
            var Q10;
            Q10=makeQuery(id+"F2.opExtrude","CAP_EDGE",EDGE,{"disambiguationData":[OSD([sQuery(id+"F1.wireOp",EDGE,"E6.1.0.0")])],"isStart":true});
            var Q11;
            Q11=makeQuery(id+"F2.opExtrude","CAP_EDGE",EDGE,{"disambiguationData":[OSD([sQuery(id+"F1.wireOp",EDGE,"E6.1.0.3")])],"isStart":true});
            var Q12;
            Q12=makeQuery(id+"F2.opExtrude","CAP_EDGE",EDGE,{"disambiguationData":[OSD([sQuery(id+"F1.wireOp",EDGE,"E6.2.0.0")])],"isStart":true});
            var Q13;
            Q13=makeQuery(id+"F2.opExtrude","CAP_EDGE",EDGE,{"disambiguationData":[OSD([sQuery(id+"F1.wireOp",EDGE,"E6.2.0.3")])],"isStart":true});
            var Q14;
            Q14=makeQuery(id+"F2.opExtrude","CAP_EDGE",EDGE,{"disambiguationData":[OSD([sQuery(id+"F1.wireOp",EDGE,"E6.3.0.0")])],"isStart":true});
            var Q15;
            Q15=makeQuery(id+"F2.opExtrude","CAP_EDGE",EDGE,{"disambiguationData":[OSD([sQuery(id+"F1.wireOp",EDGE,"E6.3.0.3")])],"isStart":true});
            fillet(context, id + "F9", {"entities" : qUnion([Q0, Q1, Q2, Q3, Q4, Q5, Q6, Q7, Q8, Q9, Q10, Q11, Q12, Q13, Q14, Q15]), "radius" : 1.5 * mm, "tangentPropagation" : true, "allowEdgeOverflow" : false});
        }
        {
            var Q0;
            Q0=makeQuery(id+"F2.opExtrude","SWEPT_EDGE",EDGE,{"disambiguationData":[OSD([sQuery(id+"F1.wireOp",EDGE,"E5.right"),sQuery(id+"F1.wireOp",EDGE,"E7.top")])]});
            var Q1;
            Q1=makeQuery(id+"F2.opExtrude","SWEPT_EDGE",EDGE,{"disambiguationData":[OSD([sQuery(id+"F1.wireOp",EDGE,"E6.1.0.3"),sQuery(id+"F1.wireOp",EDGE,"E7.top")])]});
            var Q2;
            Q2=makeQuery(id+"F2.opExtrude","SWEPT_EDGE",EDGE,{"disambiguationData":[OSD([sQuery(id+"F1.wireOp",EDGE,"E6.2.0.3"),sQuery(id+"F1.wireOp",EDGE,"E7.top")])]});
            var Q3;
            Q3=makeQuery(id+"F2.opExtrude","SWEPT_EDGE",EDGE,{"disambiguationData":[OSD([sQuery(id+"F1.wireOp",EDGE,"E6.3.0.3"),sQuery(id+"F1.wireOp",EDGE,"E7.top")])]});
            var Q4;
            Q4=makeQuery(id+"F2.opExtrude","SWEPT_EDGE",EDGE,{"disambiguationData":[OSD([sQuery(id+"F1.wireOp",EDGE,"E6.3.0.0"),sQuery(id+"F1.wireOp",EDGE,"E7.top")])]});
            var Q5;
            Q5=makeQuery(id+"F2.opExtrude","SWEPT_EDGE",EDGE,{"disambiguationData":[OSD([sQuery(id+"F1.wireOp",EDGE,"E6.2.0.0"),sQuery(id+"F1.wireOp",EDGE,"E7.top")])]});
            var Q6;
            Q6=makeQuery(id+"F2.opExtrude","SWEPT_EDGE",EDGE,{"disambiguationData":[OSD([sQuery(id+"F1.wireOp",EDGE,"E6.1.0.0"),sQuery(id+"F1.wireOp",EDGE,"E7.top")])]});
            var Q7;
            Q7=makeQuery(id+"F2.opExtrude","SWEPT_EDGE",EDGE,{"disambiguationData":[OSD([sQuery(id+"F1.wireOp",EDGE,"E5.left"),sQuery(id+"F1.wireOp",EDGE,"E7.top")])]});
            fillet(context, id + "F10", {"entities" : qUnion([Q0, Q1, Q2, Q3, Q4, Q5, Q6, Q7]), "radius" : 1.5 * mm, "tangentPropagation" : true, "allowEdgeOverflow" : false});
        }
        {
            var Q0;
            Q0=makeQuery(id+"F5.opExtrude","CAP_FACE",FACE,{"disambiguationData":[OSD([sQuery(id+"F4.wireOp",EDGE,"E9.bottom"),sQuery(id+"F4.wireOp",EDGE,"E9.top"),sQuery(id+"F4.wireOp",EDGE,"E9.left"),sQuery(id+"F4.wireOp",EDGE,"E9.right")])],"isStart":true});
            var sketch = newSketch(context, id + "F11", { "sketchPlane" : qUnion([Q0])});
            skCircle(sketch, "E10", {"center": v(-10, 66.18) * mm, "radius": 2.5 * mm});
            skSolve(sketch);
        }
        {
            var Q0;
            Q0=makeQuery(id+"F11.imprint","IMPRINT",FACE,{"disambiguationData":[TD([[makeQuery(id+"F11.imprint","IMPRINT",EDGE,{"derivedFrom":sQuery(id+"F11.wireOp",EDGE,"E10")}),1.0]])]});
            extrude(context, id + "F12", {"entities" : qUnion([Q0]), "operationType" : NewBodyOperationType.REMOVE, "oppositeDirection" : true, "depth" : 1 * mm});
        }
    });
